# Revit family: Холодильные шкафы с металлическими дверьми
name_source: partatom
category: Оборудование
units: mm (PartAtom-declared; Revit-internal decimal feet)

## family parameters
Всегда вертикально = Да
Классификация = Нет
На основе рабочей плоскости = Нет
Общий = Нет
При загрузке вырезать с полостями = Нет
Размер круглого соединителя = Использовать диаметр
Тип детали = Нормальный
Точка расчета площади = Нет

## types (23) — shared parameters
Допустимая нагрузка на полку, кг = 40
Замок = +
Клапан Шредера = +
Колесные опоры = опция
Подсветка = +
Расположение агрегата = верхнее
Система электропитания, В/Гц = 230/50
Терморегулятор = эл. блок
Тип охлаждения = динамический
Условия окр. среды (темп./влажн.) = до +40/до 80
Холодильный шкаф = <По категории>
zero-valued in all types: Отметка по умолчанию

## per-type parameters (varying)
- CM105-Sm: 1 дверь S=Нет; 1 дверь S (шир)=Нет; 1 дверь Sm=Да; 1 дверь Sm (шир)=Нет; 2  дверь S (шир)=Нет; 2 дверь S=Нет; 2 дверь Sm=Нет; 2 дверь Sm (шир)=Нет; Вес нетто/брутто, кг=95/114; Высота=1960 мм; Габаритные размеры, мм=697*695*1960; Глубина=695 мм; Диап. рабочих темп.=0....+6; Кол-во полок=4; Корпус=цельнозаливной; Материал обшивок корпуса=сталь с полимерным покрытием; Микропереключатель=клавишный; Объем, л=500; Панель S=Нет; Панель Sm=Да; Педаль=+; Потребляемая мощность, Вт=350; Размер полки, мм=595х455; Размеры в упаковке, мм=790x744x2125; Расход электроэнергии за сутки, кВт/ч=3,5; Тип оттайки=авт. с системой исп. конденсата; Хладагент=R134a; Цена, руб.=47 000; Ширина=697 мм
- CM107-Sm: 1 дверь S=Нет; 1 дверь S (шир)=Нет; 1 дверь Sm=Да; 1 дверь Sm (шир)=Нет; 2  дверь S (шир)=Нет; 2 дверь S=Нет; 2 дверь Sm=Нет; 2 дверь Sm (шир)=Нет; Вес нетто/брутто, кг=112/137; Высота=1960 мм; Габаритные размеры, мм=697*925*1960; Глубина=925 мм; Диап. рабочих темп.=0....+6; Кол-во полок=4; Корпус=цельнозаливной; Материал обшивок корпуса=сталь с полимерным покрытием; Микропереключатель=клавишный; Объем, л=700; Панель S=Нет; Панель Sm=Да; Педаль=+; Потребляемая мощность, Вт=350; Размер полки, мм=530х650; Размеры в упаковке, мм=790x988x2125; Расход электроэнергии за сутки, кВт/ч=3,5; Тип оттайки=авт. с системой исп. конденсата; Хладагент=R134a; Цена, руб.=50 500; Ширина=697 мм
- CV105-Sm: 1 дверь S=Нет; 1 дверь S (шир)=Нет; 1 дверь Sm=Да; 1 дверь Sm (шир)=Нет; 2  дверь S (шир)=Нет; 2 дверь S=Нет; 2 дверь Sm=Нет; 2 дверь Sm (шир)=Нет; Вес нетто/брутто, кг=95/114; Высота=1960 мм; Габаритные размеры, мм=697*695*1960; Глубина=695 мм; Диап. рабочих темп.=-5....+5; Кол-во полок=4; Корпус=цельнозаливной; Материал обшивок корпуса=сталь с полимерным покрытием; Микропереключатель=клавишный; Объем, л=500; Панель S=Нет; Панель Sm=Да; Педаль=+; Потребляемая мощность, Вт=400; Размер полки, мм=595х455; Размеры в упаковке, мм=790x744x2125; Расход электроэнергии за сутки, кВт/ч=4; Тип оттайки=авт., при помощи ТЭНов, с системой исп. конденсата; Хладагент=R134a; Цена, руб.=58 580; Ширина=697 мм
- CV107-Sm: 1 дверь S=Нет; 1 дверь S (шир)=Нет; 1 дверь Sm=Да; 1 дверь Sm (шир)=Нет; 2  дверь S (шир)=Нет; 2 дверь S=Нет; 2 дверь Sm=Нет; 2 дверь Sm (шир)=Нет; Вес нетто/брутто, кг=112/137; Высота=1960 мм; Габаритные размеры, мм=697*925*1960; Глубина=925 мм; Диап. рабочих темп.=-5....+5; Кол-во полок=4; Корпус=цельнозаливной; Материал обшивок корпуса=сталь с полимерным покрытием; Микропереключатель=клавишный; Объем, л=700; Панель S=Нет; Панель Sm=Да; Педаль=+; Потребляемая мощность, Вт=400; Размер полки, мм=530х650; Размеры в упаковке, мм=790x988x2125; Расход электроэнергии за сутки, кВт/ч=4,5; Тип оттайки=авт., при помощи ТЭНов, с системой исп. конденсата; Хладагент=R134a; Цена, руб.=62 620; Ширина=697 мм
- CB105-Sm: 1 дверь S=Нет; 1 дверь S (шир)=Нет; 1 дверь Sm=Да; 1 дверь Sm (шир)=Нет; 2  дверь S (шир)=Нет; 2 дверь S=Нет; 2 дверь Sm=Нет; 2 дверь Sm (шир)=Нет; Вес нетто/брутто, кг=125/149; Высота=1960 мм; Габаритные размеры, мм=697*695*1960; Глубина=695 мм; Диап. рабочих темп.=не выше -18; Кол-во полок=4; Корпус=цельнозаливной; Материал обшивок корпуса=сталь с полимерным покрытием; Микропереключатель=клавишный; Объем, л=500; Панель S=Нет; Панель Sm=Да; Педаль=+; Потребляемая мощность, Вт=550/400; Размер полки, мм=595х455; Размеры в упаковке, мм=790x988x2125; Расход электроэнергии за сутки, кВт/ч=12; Тип оттайки=авт., при помощи ТЭНов, с системой исп. конденсата; Хладагент=R404А; Цена, руб.=65 650; Ширина=697 мм
- CB107-Sm: 1 дверь S=Нет; 1 дверь S (шир)=Нет; 1 дверь Sm=Нет; 1 дверь Sm (шир)=Да; 2  дверь S (шир)=Нет; 2 дверь S=Нет; 2 дверь Sm=Нет; 2 дверь Sm (шир)=Нет; Вес нетто/брутто, кг=125/149; Высота=1996 мм; Габаритные размеры, мм=735*960*1996; Глубина=960 мм; Диап. рабочих темп.=не выше -18; Кол-во полок=4; Корпус=цельнозаливной; Материал обшивок корпуса=сталь с полимерным покрытием; Микропереключатель=клавишный; Объем, л=700; Панель S=Нет; Панель Sm=Да; Педаль=+; Потребляемая мощность, Вт=550/400; Размер полки, мм=530х650; Размеры в упаковке, мм=790x988x2125; Расход электроэнергии за сутки, кВт/ч=12; Тип оттайки=авт., при помощи ТЭНов, с системой исп. конденсата; Хладагент=R404А; Цена, руб.=72 270; Ширина=735 мм
- CM110-Sm: 1 дверь S=Нет; 1 дверь S (шир)=Нет; 1 дверь Sm=Да; 1 дверь Sm (шир)=Нет; 2  дверь S (шир)=Нет; 2 дверь S=Нет; 2 дверь Sm=Да; 2 дверь Sm (шир)=Нет; Вес нетто/брутто, кг=155/182; Высота=1960 мм; Габаритные размеры, мм=1402*695*1960; Глубина=695 мм; Диап. рабочих темп.=0....+6; Кол-во полок=8; Корпус=цельнозаливной; Материал обшивок корпуса=сталь с полимерным покрытием; Микропереключатель=клавишный; Объем, л=1000; Панель S=Нет; Панель Sm=Да; Педаль=+; Потребляемая мощность, Вт=550; Размер полки, мм=595х455; Размеры в упаковке, мм=1490x744x2125; Расход электроэнергии за сутки, кВт/ч=5.5; Тип оттайки=авт. с системой исп. конденсата; Хладагент=R134a; Цена, руб.=65 600; Ширина=1402 мм
- CM114-Sm: 1 дверь S=Нет; 1 дверь S (шир)=Нет; 1 дверь Sm=Да; 1 дверь Sm (шир)=Нет; 2  дверь S (шир)=Нет; 2 дверь S=Нет; 2 дверь Sm=Да; 2 дверь Sm (шир)=Нет; Вес нетто/брутто, кг=184/214; Высота=1960 мм; Габаритные размеры, мм=1402*925*1960; Глубина=925 мм; Диап. рабочих темп.=0....+6; Кол-во полок=8; Корпус=цельнозаливной; Материал обшивок корпуса=сталь с полимерным покрытием; Микропереключатель=клавишный; Объем, л=1400; Панель S=Нет; Панель Sm=Да; Педаль=+; Потребляемая мощность, Вт=550; Размер полки, мм=530х650; Размеры в упаковке, мм=1490x988x2125; Расход электроэнергии за сутки, кВт/ч=6; Тип оттайки=авт. с системой исп. конденсата; Хладагент=R134a; Цена, руб.=71 700; Ширина=1402 мм
- CV110-Sm: 1 дверь S=Нет; 1 дверь S (шир)=Нет; 1 дверь Sm=Да; 1 дверь Sm (шир)=Нет; 2  дверь S (шир)=Нет; 2 дверь S=Нет; 2 дверь Sm=Да; 2 дверь Sm (шир)=Нет; Вес нетто/брутто, кг=155/182; Высота=1960 мм; Габаритные размеры, мм=1402*695*1960; Глубина=695 мм; Диап. рабочих темп.=-5....+5; Кол-во полок=8; Корпус=цельнозаливной; Материал обшивок корпуса=сталь с полимерным покрытием; Микропереключатель=клавишный; Объем, л=1000; Панель S=Нет; Панель Sm=Да; Педаль=+; Потребляемая мощность, Вт=630; Размер полки, мм=595х455; Размеры в упаковке, мм=1490x988x2125; Расход электроэнергии за сутки, кВт/ч=6; Тип оттайки=авт., при помощи ТЭНов, с системой исп. конденсата; Хладагент=R134a; Цена, руб.=76 600; Ширина=1402 мм
- CV114-Sm: 1 дверь S=Нет; 1 дверь S (шир)=Нет; 1 дверь Sm=Да; 1 дверь Sm (шир)=Нет; 2  дверь S (шир)=Нет; 2 дверь S=Нет; 2 дверь Sm=Да; 2 дверь Sm (шир)=Нет; Вес нетто/брутто, кг=184/214; Высота=1960 мм; Габаритные размеры, мм=1402*925*1960; Глубина=925 мм; Диап. рабочих темп.=-5....+5; Кол-во полок=8; Корпус=цельнозаливной; Материал обшивок корпуса=сталь с полимерным покрытием; Микропереключатель=клавишный; Объем, л=1400; Панель S=Нет; Панель Sm=Да; Педаль=+; Потребляемая мощность, Вт=630; Размер полки, мм=530х650; Размеры в упаковке, мм=1490x988x2125; Расход электроэнергии за сутки, кВт/ч=6.5; Тип оттайки=авт., при помощи ТЭНов, с системой исп. конденсата; Хладагент=R134a; Цена, руб.=84 990; Ширина=1402 мм
- CM105-S: 1 дверь S=Да; 1 дверь S (шир)=Нет; 1 дверь Sm=Нет; 1 дверь Sm (шир)=Нет; 2  дверь S (шир)=Нет; 2 дверь S=Нет; 2 дверь Sm=Нет; 2 дверь Sm (шир)=Нет; Вес нетто/брутто, кг=95/114; Высота=1960 мм; Габаритные размеры, мм=697*695*1960; Глубина=695 мм; Диап. рабочих темп.=0....+6; Кол-во полок=4; Корпус=-; Материал обшивок корпуса=-; Микропереключатель=-; Объем, л=500; Панель S=Да; Панель Sm=Нет; Педаль=+; Потребляемая мощность, Вт=350; Размер полки, мм=595х455; Размеры в упаковке, мм=790x744x2125; Расход электроэнергии за сутки, кВт/ч=3,5; Тип оттайки=авт., при помощи ТЭНов, с системой исп. конденсата; Хладагент=R134a; Цена, руб.=41 400; Ширина=697 мм
- CM107-S: 1 дверь S=Да; 1 дверь S (шир)=Нет; 1 дверь Sm=Нет; 1 дверь Sm (шир)=Нет; 2  дверь S (шир)=Нет; 2 дверь S=Нет; 2 дверь Sm=Нет; 2 дверь Sm (шир)=Нет; Вес нетто/брутто, кг=112/137; Высота=1960 мм; Габаритные размеры, мм=697*925*1960; Глубина=925 мм; Диап. рабочих темп.=0....+6; Кол-во полок=4; Корпус=цельнозаливной; Материал обшивок корпуса=-; Микропереключатель=-; Объем, л=700; Панель S=Да; Панель Sm=Нет; Педаль=-; Потребляемая мощность, Вт=350; Размер полки, мм=530х650; Размеры в упаковке, мм=790x988x2125; Расход электроэнергии за сутки, кВт/ч=4; Тип оттайки=авт. с системой исп. конденсата; Хладагент=R134a; Цена, руб.=45 000; Ширина=697 мм
- CM110-S: 1 дверь S=Да; 1 дверь S (шир)=Нет; 1 дверь Sm=Нет; 1 дверь Sm (шир)=Нет; 2  дверь S (шир)=Нет; 2 дверь S=Да; 2 дверь Sm=Нет; 2 дверь Sm (шир)=Нет; Вес нетто/брутто, кг=155/182; Высота=1960 мм; Габаритные размеры, мм=1402*695*1960; Глубина=695 мм; Диап. рабочих темп.=0....+6; Кол-во полок=8; Корпус=цельнозаливной; Материал обшивок корпуса=сталь с полимерным покрытием; Микропереключатель=клавишный; Объем, л=1000; Панель S=Да; Панель Sm=Нет; Педаль=+; Потребляемая мощность, Вт=550; Размер полки, мм=595х455; Размеры в упаковке, мм=1490x744x2125; Расход электроэнергии за сутки, кВт/ч=5.5; Тип оттайки=авт. с системой исп. конденсата; Хладагент=R134a; Цена, руб.=65 600; Ширина=1402 мм
- CB114-Sm: 1 дверь S=Нет; 1 дверь S (шир)=Нет; 1 дверь Sm=Нет; 1 дверь Sm (шир)=Да; 2  дверь S (шир)=Нет; 2 дверь S=Нет; 2 дверь Sm=Нет; 2 дверь Sm (шир)=Да; Вес нетто/брутто, кг=212/242; Высота=1996 мм; Габаритные размеры, мм=1474*960*1996; Глубина=960 мм; Диап. рабочих темп.=не выше -18; Кол-во полок=4; Корпус=цельнозаливной; Материал обшивок корпуса=сталь с полимерным покрытием; Микропереключатель=клавишный; Объем, л=1400; Панель S=Нет; Панель Sm=Да; Педаль=+; Потребляемая мощность, Вт=800/1200; Размер полки, мм=530х650; Размеры в упаковке, мм=1550x988x2160; Расход электроэнергии за сутки, кВт/ч=20.5; Тип оттайки=авт., при помощи ТЭНов, с системой исп. конденсата; Хладагент=R404А; Цена, руб.=101 900; Ширина=1474 мм
- CB107-S: 1 дверь S=Нет; 1 дверь S (шир)=Да; 1 дверь Sm=Нет; 1 дверь Sm (шир)=Нет; 2  дверь S (шир)=Нет; 2 дверь S=Нет; 2 дверь Sm=Нет; 2 дверь Sm (шир)=Нет; Вес нетто/брутто, кг=125/149; Высота=1996 мм; Габаритные размеры, мм=735*960*1996; Глубина=960 мм; Диап. рабочих темп.=не выше -18; Кол-во полок=4; Корпус=цельнозаливной; Материал обшивок корпуса=-; Микропереключатель=-; Объем, л=700; Панель S=Да; Панель Sm=Нет; Педаль=-; Потребляемая мощность, Вт=550/400; Размер полки, мм=530х650; Размеры в упаковке, мм=850x988x2160; Расход электроэнергии за сутки, кВт/ч=12; Тип оттайки=авт., при помощи ТЭНов, с системой исп. конденсата; Хладагент=R134a; Цена, руб.=62 800; Ширина=735 мм
- CV105-S: 1 дверь S=Да; 1 дверь S (шир)=Нет; 1 дверь Sm=Нет; 1 дверь Sm (шир)=Нет; 2  дверь S (шир)=Нет; 2 дверь S=Нет; 2 дверь Sm=Нет; 2 дверь Sm (шир)=Нет; Вес нетто/брутто, кг=96/115; Высота=1960 мм; Габаритные размеры, мм=697*695*1960; Глубина=695 мм; Диап. рабочих темп.=-5....+5; Кол-во полок=4; Корпус=цельнозаливной; Материал обшивок корпуса=сталь с полимерным покрытием; Микропереключатель=клавишный; Объем, л=500; Панель S=Да; Панель Sm=Нет; Педаль=+; Потребляемая мощность, Вт=400; Размер полки, мм=595х455; Размеры в упаковке, мм=790x744x2125; Расход электроэнергии за сутки, кВт/ч=4; Тип оттайки=авт. с системой исп. конденсата; Хладагент=R134a; Цена, руб.=52 200; Ширина=697 мм
- CV107-S: 1 дверь S=Да; 1 дверь S (шир)=Нет; 1 дверь Sm=Нет; 1 дверь Sm (шир)=Нет; 2  дверь S (шир)=Нет; 2 дверь S=Нет; 2 дверь Sm=Нет; 2 дверь Sm (шир)=Нет; Вес нетто/брутто, кг=113/138; Высота=1960 мм; Габаритные размеры, мм=697*925*1960; Глубина=925 мм; Диап. рабочих темп.=-5....+5; Кол-во полок=4; Корпус=цельнозаливной; Материал обшивок корпуса=сталь с полимерным покрытием; Микропереключатель=клавишный; Объем, л=700; Панель S=Да; Панель Sm=Нет; Педаль=+; Потребляемая мощность, Вт=400; Размер полки, мм=530х650; Размеры в упаковке, мм=790x988x2125; Расход электроэнергии за сутки, кВт/ч=4,5; Тип оттайки=авт., при помощи ТЭНов, с системой исп. конденсата; Хладагент=R134a; Цена, руб.=56 000; Ширина=697 мм
- CV110-S: 1 дверь S=Да; 1 дверь S (шир)=Нет; 1 дверь Sm=Нет; 1 дверь Sm (шир)=Нет; 2  дверь S (шир)=Нет; 2 дверь S=Да; 2 дверь Sm=Нет; 2 дверь Sm (шир)=Нет; Вес нетто/брутто, кг=155/184; Высота=1960 мм; Габаритные размеры, мм=1402*695*1960; Глубина=695 мм; Диап. рабочих темп.=-5....+5; Кол-во полок=8; Корпус=цельнозаливной; Материал обшивок корпуса=сталь с полимерным покрытием; Микропереключатель=клавишный; Объем, л=1000; Панель S=Да; Панель Sm=Нет; Педаль=+; Потребляемая мощность, Вт=630; Размер полки, мм=595х455; Размеры в упаковке, мм=1490x988x2125; Расход электроэнергии за сутки, кВт/ч=6; Тип оттайки=авт., при помощи ТЭНов, с системой исп. конденсата; Хладагент=R134a; Цена, руб.=68 800; Ширина=1402 мм
- CV114-S: 1 дверь S=Да; 1 дверь S (шир)=Нет; 1 дверь Sm=Нет; 1 дверь Sm (шир)=Нет; 2  дверь S (шир)=Нет; 2 дверь S=Да; 2 дверь Sm=Нет; 2 дверь Sm (шир)=Нет; Вес нетто/брутто, кг=184/214; Высота=1960 мм; Габаритные размеры, мм=1402*925*1960; Глубина=925 мм; Диап. рабочих темп.=-5....+5; Кол-во полок=8; Корпус=цельнозаливной; Материал обшивок корпуса=сталь с полимерным покрытием; Микропереключатель=клавишный; Объем, л=1400; Панель S=Да; Панель Sm=Нет; Педаль=+; Потребляемая мощность, Вт=630; Размер полки, мм=530х650; Размеры в упаковке, мм=1490x988x2125; Расход электроэнергии за сутки, кВт/ч=6.5; Тип оттайки=авт. с системой исп. конденсата; Хладагент=R134a; Цена, руб.=75 200; Ширина=1402 мм
- CB114-S: 1 дверь S=Нет; 1 дверь S (шир)=Да; 1 дверь Sm=Нет; 1 дверь Sm (шир)=Нет; 2  дверь S (шир)=Да; 2 дверь S=Нет; 2 дверь Sm=Нет; 2 дверь Sm (шир)=Нет; Вес нетто/брутто, кг=212/242; Высота=1996 мм; Габаритные размеры, мм=1474*960*1996; Глубина=960 мм; Диап. рабочих темп.=не выше -18; Кол-во полок=4; Корпус=цельнозаливной; Материал обшивок корпуса=сталь с полимерным покрытием; Микропереключатель=клавишный; Объем, л=1400; Панель S=Да; Панель Sm=Нет; Педаль=+; Потребляемая мощность, Вт=800/1200; Размер полки, мм=530х650; Размеры в упаковке, мм=1550x988x2160; Расход электроэнергии за сутки, кВт/ч=20.5; Тип оттайки=авт., при помощи ТЭНов, с системой исп. конденсата; Хладагент=R404А; Цена, руб.=90 900; Ширина=1474 мм
- СС214-S: 1 дверь S=Да; 1 дверь S (шир)=Нет; 1 дверь Sm=Нет; 1 дверь Sm (шир)=Нет; 2  дверь S (шир)=Нет; 2 дверь S=Да; 2 дверь Sm=Нет; 2 дверь Sm (шир)=Нет; Вес нетто/брутто, кг=214/244; Высота=1960 мм; Габаритные размеры, мм=1402*925*1960; Глубина=925 мм; Диап. рабочих темп.=0....+6/не выше -18; Кол-во полок=8; Корпус=цельнозаливной; Материал обшивок корпуса=сталь с полимерным покрытием; Микропереключатель=клавишный; Объем, л=700+700; Панель S=Да; Панель Sm=Нет; Педаль=+; Потребляемая мощность, Вт=900; Размер полки, мм=530х650; Размеры в упаковке, мм=1490x988x2125; Расход электроэнергии за сутки, кВт/ч=14,5; Тип оттайки=авт., при помощи ТЭНов (в низкотемпературном отделении) с системой исп. конденсата; Хладагент=R134a; Цена, руб.=94 400; Ширина=1402 мм
- CM114-S: 1 дверь S=Да; 1 дверь S (шир)=Нет; 1 дверь Sm=Нет; 1 дверь Sm (шир)=Нет; 2  дверь S (шир)=Нет; 2 дверь S=Да; 2 дверь Sm=Нет; 2 дверь Sm (шир)=Нет; Вес нетто/брутто, кг=184/214; Высота=1960 мм; Габаритные размеры, мм=1402*925*1960; Глубина=925 мм; Диап. рабочих темп.=0....+6; Кол-во полок=8; Корпус=цельнозаливной; Материал обшивок корпуса=сталь с полимерным покрытием; Микропереключатель=клавишный; Объем, л=1400; Панель S=Да; Панель Sm=Нет; Педаль=+; Потребляемая мощность, Вт=550; Размер полки, мм=530х650; Размеры в упаковке, мм=1490x988x2125; Расход электроэнергии за сутки, кВт/ч=6; Тип оттайки=авт. с системой исп. конденсата; Хладагент=R134a; Цена, руб.=63 990; Ширина=1402 мм
- CB105-S: 1 дверь S=Да; 1 дверь S (шир)=Нет; 1 дверь Sm=Нет; 1 дверь Sm (шир)=Нет; 2  дверь S (шир)=Нет; 2 дверь S=Нет; 2 дверь Sm=Нет; 2 дверь Sm (шир)=Нет; Вес нетто/брутто, кг=102/121; Высота=1960 мм; Габаритные размеры, мм=697*695*1960; Глубина=695 мм; Диап. рабочих темп.=не выше -18; Кол-во полок=4; Корпус=цельнозаливной; Материал обшивок корпуса=сталь с полимерным покрытием; Микропереключатель=клавишный; Объем, л=500; Панель S=Да; Панель Sm=Нет; Педаль=+; Потребляемая мощность, Вт=550/400; Размер полки, мм=595х455; Размеры в упаковке, мм=790x744x2125; Расход электроэнергии за сутки, кВт/ч=12; Тип оттайки=авт., при помощи ТЭНов, с системой исп. конденсата; Хладагент=R404А; Цена, руб.=56 300; Ширина=697 мм
